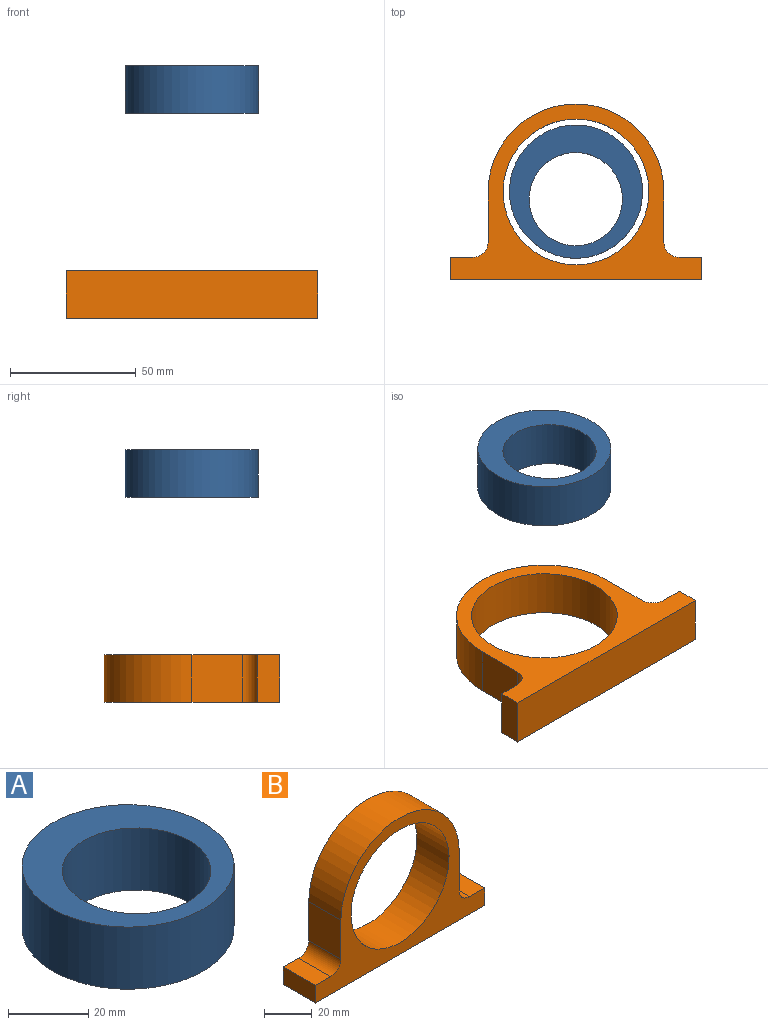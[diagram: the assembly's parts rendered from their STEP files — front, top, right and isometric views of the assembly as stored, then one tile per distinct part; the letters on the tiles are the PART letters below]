
ASSEMBLY  parts=2 mates=1
PART A: 4 faces, bbox 53x53x19 mm
  f0: cylinder r=26.5mm len=53mm, axis (0,0,-1), area 3163.6mm2, adj f1,f2
  f1: plane 53x53mm, normal (0,0,1), area 1124.6mm2, adj f0,f3
  f2: plane 53x53mm, normal (0,0,-1), area 1124.6mm2, adj f0,f3
  f3: cylinder r=18.55mm len=37.11mm, axis (0,0,1), area 2215.1mm2, adj f1,f2
PART B: 13 faces, bbox 100x19x70 mm
  f0: plane 19x9mm, normal (0,0,1), area 171mm2, adj f7,f9,f10,f11
  f1: plane 20x19mm, normal (1,0,0), area 380mm2, adj f2,f9,f10,f11
  f2: cylinder r=35mm len=70mm, axis (0,1,0), area 2089.2mm2, adj f1,f3,f9,f10
  f3: plane 20x19mm, normal (-1,0,0), area 380mm2, adj f2,f9,f10,f12
  f4: plane 19x9mm, normal (0,0,1), area 171mm2, adj f5,f9,f10,f12
  f5: plane 19x9mm, normal (-1,0,0), area 171mm2, adj f4,f6,f9,f10
  f6: plane 100x19mm, normal (0,0,-1), area 1900mm2, adj f5,f7,f9,f10
  f7: plane 19x9mm, normal (1,0,0), area 171mm2, adj f0,f6,f9,f10
  f8: cylinder r=29mm len=58mm, axis (0,1,0), area 3462mm2, adj f9,f10
  f9: plane 100x70mm, normal (0,-1,0), area 2017.6mm2, adj f0,f1,f2,f3,f4,f5,f6,f7
  f10: plane 100x70mm, normal (0,1,0), area 2017.6mm2, adj f0,f1,f2,f3,f4,f5,f6,f7
  f11: cylinder r=6mm len=19mm, axis (0,-1,0), area 179.1mm2, adj f0,f1,f9,f10
  f12: cylinder r=6mm len=19mm, axis (0,-1,0), area 179.1mm2, adj f3,f4,f9,f10
PLACE A rot(axis=(0,0,-1),1.9deg) t=(-24.27,38.05,10.81)mm
PLACE B rot(axis=(-1,0,0),90deg) t=(-24.27,38.05,-70.79)mm fixed
MATE cylindrical B.f8 <-> A.f0  axis (0,0,-1) through (-24.27,38.05,-61.29)mm
